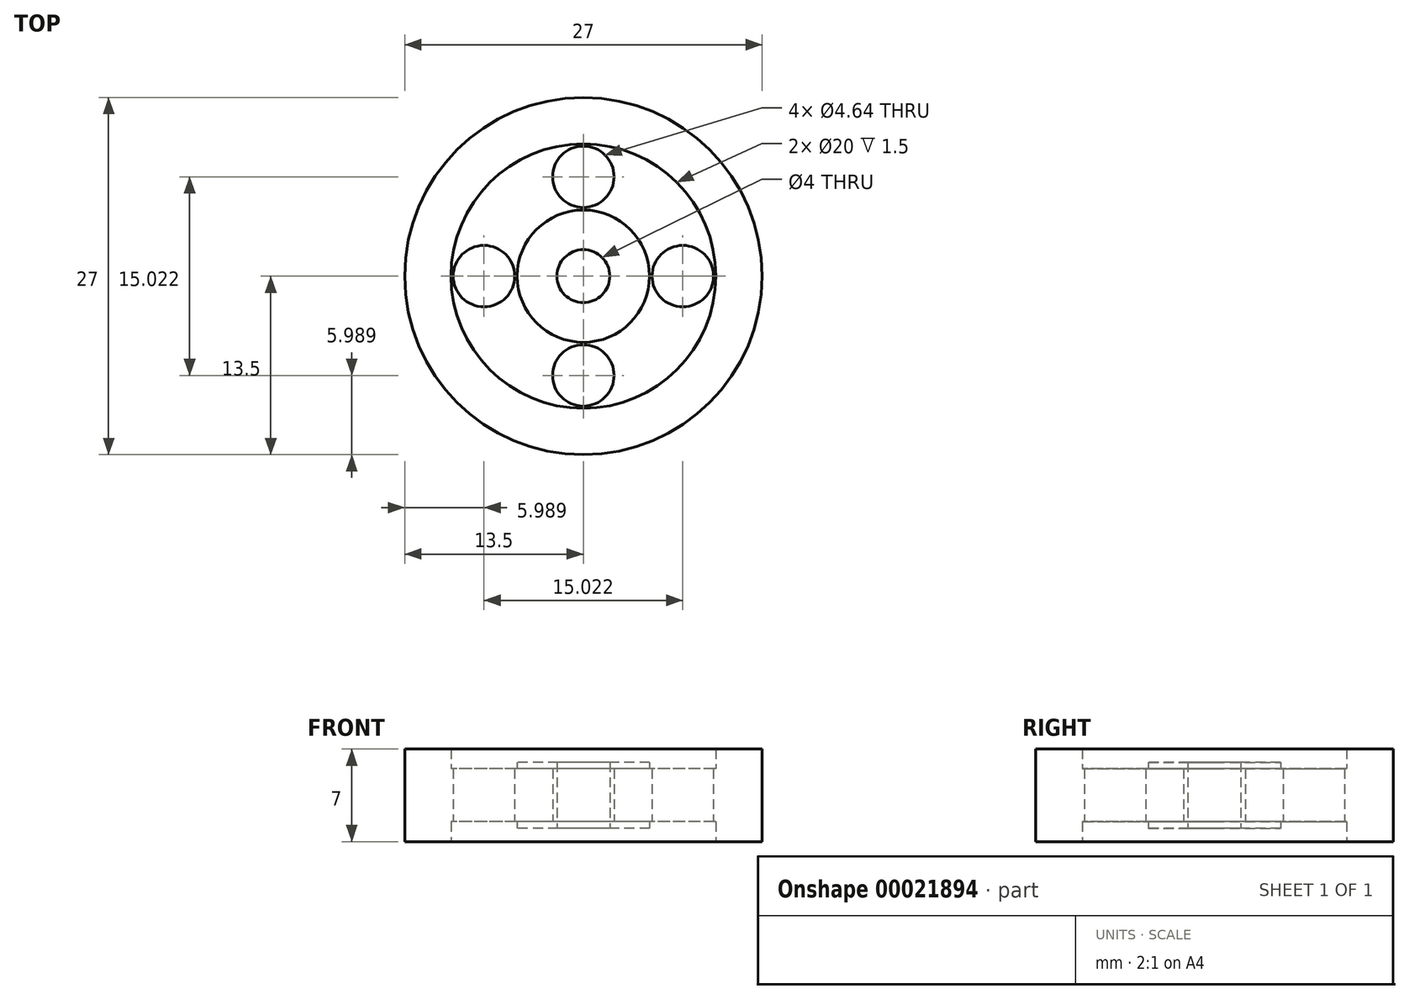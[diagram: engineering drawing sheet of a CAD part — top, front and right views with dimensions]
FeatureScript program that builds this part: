
annotation { "Feature Type Name" : "Feature", "Feature Type Description" : "" }
export const myFeature = defineFeature(function(context is Context, id is Id, definition is map)
    precondition{}
    {
        {
            var Q0;
            Q0=qCreatedBy(makeId("Top.planeOp"),FACE);
            var sketch = newSketch(context, id + "F0", { "sketchPlane" : qUnion([Q0])});
            skCircle(sketch, "E0", {"center": v(0, 0) * mm, "radius": 2 * mm});
            skCircle(sketch, "E1", {"center": v(0, 0) * mm, "radius": 5 * mm});
            skCircle(sketch, "E2", {"center": v(0, 0) * mm, "radius": 10 * mm});
            skLineSegment(sketch, "E3", {"start": v(0, 0) * mm, "end": v(0, 10) * mm});
            skCircle(sketch, "E4", {"center": v(0, 7.51) * mm, "radius": 2.32 * mm});
            skCircle(sketch, "E5.1.0", {"center": v(-7.51, 0) * mm, "radius": 2.32 * mm});
            skCircle(sketch, "E5.2.0", {"center": v(0, -7.51) * mm, "radius": 2.32 * mm});
            skCircle(sketch, "E5.3.0", {"center": v(7.51, 0) * mm, "radius": 2.32 * mm});
            skCircle(sketch, "E6", {"center": v(0, 0) * mm, "radius": 13.5 * mm});
            skSolve(sketch);
        }
        {
            var Q0;
            Q0=makeQuery(id+"F0.imprint","IMPRINT",FACE,{"disambiguationData":[TD([[makeQuery(id+"F0.imprint","IMPRINT",EDGE,{"derivedFrom":sQuery(id+"F0.wireOp",EDGE,"E2")}),-1.0]])]});
            extrude(context, id + "F1", {"entities" : qUnion([Q0]), "endBound" : BoundingType.SYMMETRIC, "depth" : 7 * mm});
        }
        {
            var Q0;
            Q0=makeQuery(id+"F0.imprint","IMPRINT",FACE,{"disambiguationData":[TD([[makeQuery(id+"F0.imprint","IMPRINT",EDGE,{"derivedFrom":sQuery(id+"F0.wireOp",EDGE,"E1")}),-1.0]])]});
            extrude(context, id + "F2", {"entities" : qUnion([Q0]), "operationType" : NewBodyOperationType.ADD, "endBound" : BoundingType.SYMMETRIC, "depth" : 4 * mm});
        }
        {
            var Q0;
            Q0=makeQuery(id+"F0.imprint","IMPRINT",FACE,{"disambiguationData":[TD([[makeQuery(id+"F0.imprint","IMPRINT",EDGE,{"derivedFrom":sQuery(id+"F0.wireOp",EDGE,"E0")}),-1.0]])]});
            extrude(context, id + "F3", {"entities" : qUnion([Q0]), "operationType" : NewBodyOperationType.ADD, "endBound" : BoundingType.SYMMETRIC, "depth" : 5 * mm});
        }
    });
